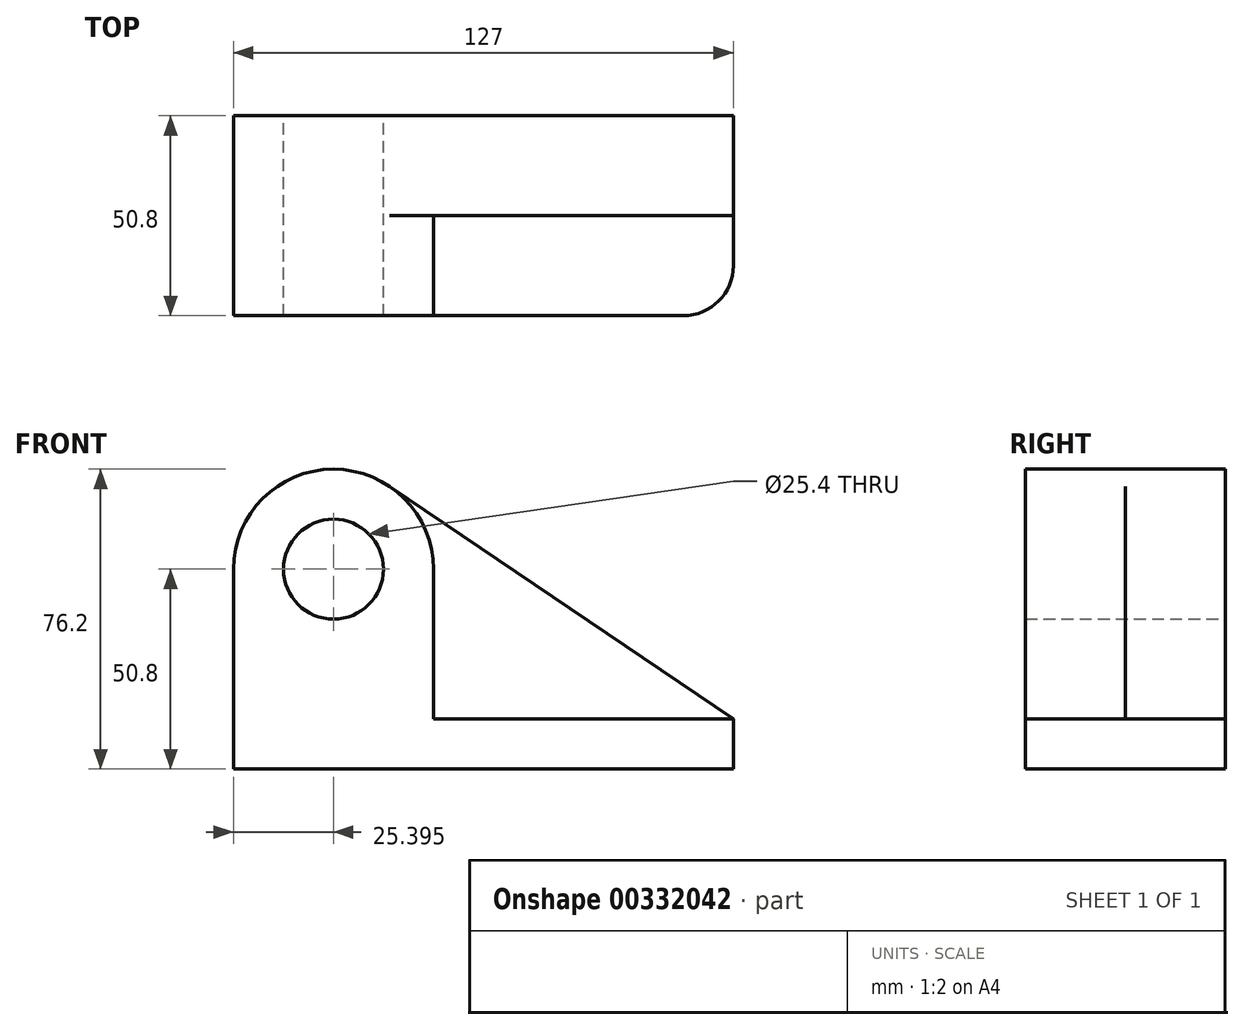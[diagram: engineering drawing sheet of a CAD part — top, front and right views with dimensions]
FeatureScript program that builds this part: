
annotation { "Feature Type Name" : "Feature", "Feature Type Description" : "" }
export const myFeature = defineFeature(function(context is Context, id is Id, definition is map)
    precondition{}
    {
        {
            var Q0;
            Q0=qCreatedBy(makeId("Front.planeOp"),FACE);
            var sketch = newSketch(context, id + "F0", { "sketchPlane" : qUnion([Q0])});
            skCircle(sketch, "E0", {"center": v(-40.6, 38.1) * mm, "radius": 12.7 * mm});
            skArc(sketch, "E1", {"start": v(-26.37, 59.13) * mm, "mid": v(-52.51, 60.54) * mm, "end": v(-66, 38.1) * mm});
            skLineSegment(sketch, "E2", {"start": v(-66, 38.1) * mm, "end": v(-66, -12.7) * mm});
            skLineSegment(sketch, "E3", {"start": v(-66, -12.7) * mm, "end": v(61, -12.7) * mm});
            skLineSegment(sketch, "E4", {"start": v(61, -12.7) * mm, "end": v(61, 0) * mm});
            skLineSegment(sketch, "E5", {"start": v(61, 0) * mm, "end": v(-26.37, 59.13) * mm});
            skSolve(sketch);
        }
        {
            var Q0;
            Q0=makeQuery(id+"F0.imprint","IMPRINT",FACE,{"disambiguationData":[TD([[makeQuery(id+"F0.imprint","IMPRINT",EDGE,{"derivedFrom":sQuery(id+"F0.wireOp",EDGE,"E0")}),-1.0]])]});
            extrude(context, id + "F1", {"entities" : qUnion([Q0]), "depth" : 25.4 * mm});
        }
        {
            var Q0;
            Q0=makeQuery(id+"F1.opExtrude","CAP_FACE",FACE,{"disambiguationData":[OSD([sQuery(id+"F0.wireOp",EDGE,"E0"),sQuery(id+"F0.wireOp",EDGE,"E1"),sQuery(id+"F0.wireOp",EDGE,"E2"),sQuery(id+"F0.wireOp",EDGE,"E3"),sQuery(id+"F0.wireOp",EDGE,"E4"),sQuery(id+"F0.wireOp",EDGE,"E5")])],"isStart":false});
            var sketch = newSketch(context, id + "F2", { "sketchPlane" : qUnion([Q0])});
            skCircle(sketch, "E6", {"center": v(-40.6, 38.1) * mm, "radius": 12.7 * mm});
            skArc(sketch, "E7", {"start": v(-15.41, 34.85) * mm, "mid": v(-15.2, 38.1) * mm, "end": v(-15.41, 41.35) * mm});
            skLineSegment(sketch, "E8.bottom", {"start": v(-66, -12.7) * mm, "end": v(61, -12.7) * mm});
            skLineSegment(sketch, "E8.top", {"start": v(-15.2, 0) * mm, "end": v(61, 0) * mm});
            skLineSegment(sketch, "E8.left", {"start": v(-66, -12.7) * mm, "end": v(-66, 0) * mm});
            skLineSegment(sketch, "E8.right", {"start": v(61, -12.7) * mm, "end": v(61, 0) * mm});
            skArc(sketch, "E9", {"start": v(-15.41, 34.85) * mm, "mid": v(-38.97, 63.45) * mm, "end": v(-66, 38.1) * mm});
            skLineSegment(sketch, "E10", {"start": v(-66, 38.1) * mm, "end": v(-66, 0) * mm});
            skLineSegment(sketch, "E11", {"start": v(-15.2, 38.1) * mm, "end": v(-15.2, 0) * mm});
            skPoint(sketch, "E12.orphan", {"position": v(-15.41, 0) * mm});
            skSolve(sketch);
        }
        {
            var Q0;
            Q0=makeQuery(id+"F2.imprint","IMPRINT",FACE,{"disambiguationData":[TD([[makeQuery(id+"F2.imprint","IMPRINT",EDGE,{"derivedFrom":sQuery(id+"F2.wireOp",EDGE,"E6")}),-1.0]])]});
            extrude(context, id + "F3", {"entities" : qUnion([Q0]), "operationType" : NewBodyOperationType.ADD, "depth" : 25.4 * mm});
        }
        {
            var Q0;
            Q0=makeQuery(id+"F3.opExtrude","CAP_EDGE",EDGE,{"disambiguationData":[OSD([sQuery(id+"F2.wireOp",EDGE,"E8.right")])],"isStart":false});
            fillet(context, id + "F4", {"entities" : qUnion([Q0]), "radius" : 12.7 * mm, "tangentPropagation" : true, "allowEdgeOverflow" : false});
        }
    });
